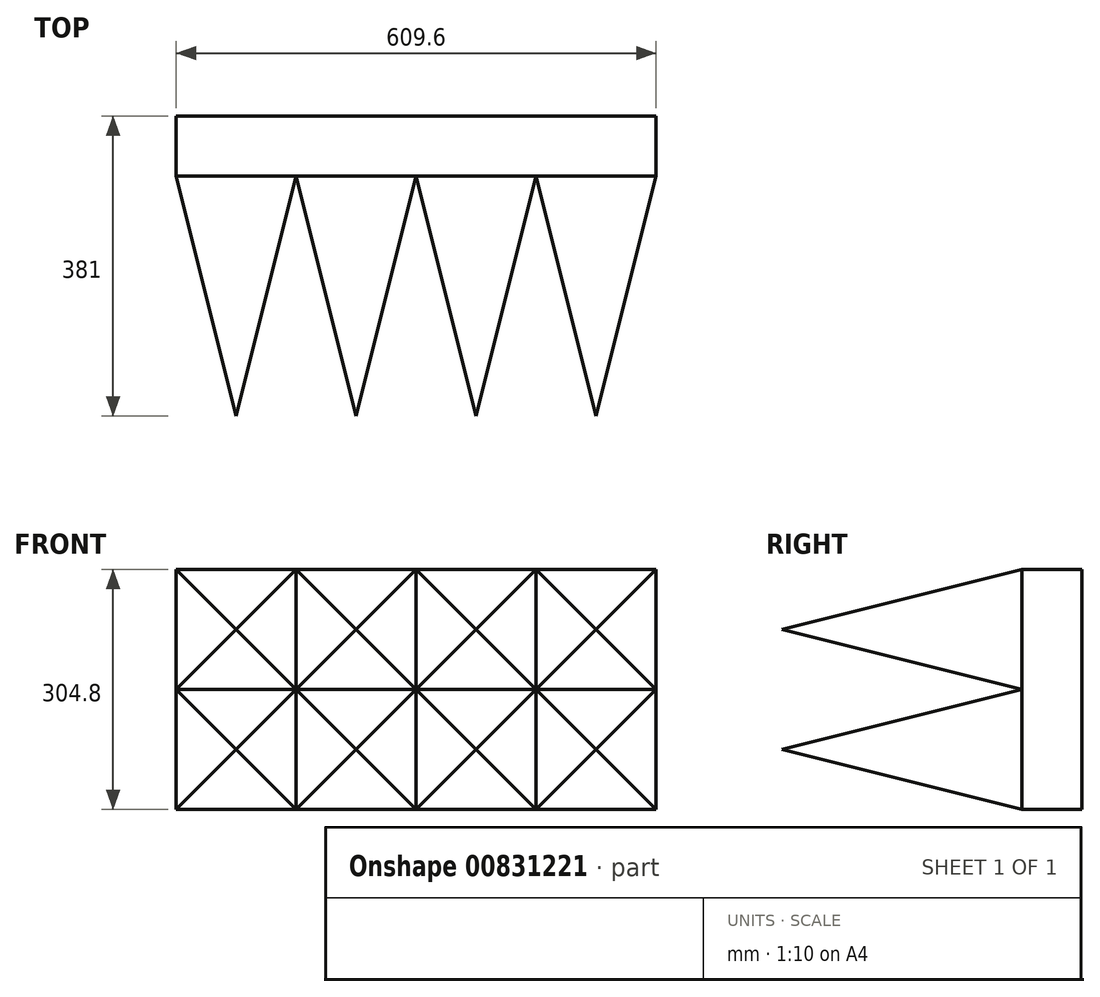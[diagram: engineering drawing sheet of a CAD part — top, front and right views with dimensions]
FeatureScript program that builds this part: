
annotation { "Feature Type Name" : "Feature", "Feature Type Description" : "" }
export const myFeature = defineFeature(function(context is Context, id is Id, definition is map)
    precondition{}
    {
        {
            var Q0;
            Q0=qCreatedBy(makeId("Front.planeOp"),FACE);
            var sketch = newSketch(context, id + "F0", { "sketchPlane" : qUnion([Q0])});
            skLineSegment(sketch, "E0.bottom", {"start": v(304.8, 152.4) * mm, "end": v(-304.8, 152.4) * mm});
            skLineSegment(sketch, "E0.top", {"start": v(304.8, -152.4) * mm, "end": v(-304.8, -152.4) * mm});
            skLineSegment(sketch, "E0.left", {"start": v(304.8, 152.4) * mm, "end": v(304.8, -152.4) * mm});
            skLineSegment(sketch, "E0.right", {"start": v(-304.8, 152.4) * mm, "end": v(-304.8, -152.4) * mm});
            skPoint(sketch, "E0.middle", {"position": v(0, 0) * mm});
            skSolve(sketch);
        }
        {
            var Q0;
            Q0=qSketchRegion(id+"F0",true);
            extrude(context, id + "F1", {"entities" : qUnion([Q0]), "depth" : 76.2 * mm});
        }
        {
            var Q0;
            Q0=qCreatedBy(makeId("Front.planeOp"),FACE);
            cPlane(context, id + "F2", {"entities" : qUnion([Q0]), "cplaneType" : CPlaneType.OFFSET, "offset" : 381 * mm, "width" : 152.4 * mm, "height" : 152.4 * mm});
        }
        {
            var Q0;
            Q0=makeQuery(id+"F1.opExtrude","CAP_FACE",FACE,{"disambiguationData":[OSD([sQuery(id+"F0.wireOp",EDGE,"E0.bottom"),sQuery(id+"F0.wireOp",EDGE,"E0.top"),sQuery(id+"F0.wireOp",EDGE,"E0.left"),sQuery(id+"F0.wireOp",EDGE,"E0.right")])],"isStart":false});
            var sketch = newSketch(context, id + "F3", { "sketchPlane" : qUnion([Q0])});
            skLineSegment(sketch, "E1.bottom", {"start": v(-152.4, 152.4) * mm, "end": v(-304.8, 152.4) * mm});
            skLineSegment(sketch, "E1.top", {"start": v(-152.4, 0) * mm, "end": v(-304.8, 0) * mm});
            skLineSegment(sketch, "E1.left", {"start": v(-152.4, 152.4) * mm, "end": v(-152.4, 0) * mm});
            skLineSegment(sketch, "E1.right", {"start": v(-304.8, 152.4) * mm, "end": v(-304.8, 0) * mm});
            skPoint(sketch, "E1.middle", {"position": v(-228.6, 76.2) * mm});
            skSolve(sketch);
        }
        {
            var Q0;
            Q0=qCreatedBy(id+"F2.planeOp",FACE);
            var sketch = newSketch(context, id + "F4", { "sketchPlane" : qUnion([Q0])});
            skPoint(sketch, "E2.0", {"position": v(-228.6, 76.2) * mm});
            skSolve(sketch);
        }
        {
            var Q1;
            Q1=makeQuery(id+"F3.imprint","IMPRINT",FACE,{"disambiguationData":[TD([[makeQuery(id+"F3.imprint","IMPRINT",EDGE,{"derivedFrom":sQuery(id+"F3.wireOp",EDGE,"E1.bottom")}),1.0]])]});
            var Q2;
            Q2=sQuery(id+"F4.wireOp",VERTEX,"E2.0");
            loft(context, id + "F5", {"operationType" : NewBodyOperationType.ADD, "sheetProfilesArray" : [{ "sheetProfileEntities" : qUnion([Q1]) }, { "sheetProfileEntities" : qUnion([Q2]) }]});
        }
        {
            var Q0;
            Q0=makeQuery(id+"F1.opExtrude","CAP_FACE",FACE,{"disambiguationData":[OSD([sQuery(id+"F0.wireOp",EDGE,"E0.bottom"),sQuery(id+"F0.wireOp",EDGE,"E0.top"),sQuery(id+"F0.wireOp",EDGE,"E0.left"),sQuery(id+"F0.wireOp",EDGE,"E0.right")])],"isStart":false});
            var sketch = newSketch(context, id + "F6", { "sketchPlane" : qUnion([Q0])});
            skLineSegment(sketch, "E3.bottom", {"start": v(0, 152.4) * mm, "end": v(-152.4, 152.4) * mm});
            skLineSegment(sketch, "E3.top", {"start": v(0, 0) * mm, "end": v(-152.4, 0) * mm});
            skLineSegment(sketch, "E3.left", {"start": v(0, 152.4) * mm, "end": v(0, 0) * mm});
            skLineSegment(sketch, "E3.right", {"start": v(-152.4, 152.4) * mm, "end": v(-152.4, 0) * mm});
            skPoint(sketch, "E3.middle", {"position": v(-76.2, 76.2) * mm});
            skSolve(sketch);
        }
        {
            var Q0;
            Q0=qCreatedBy(id+"F2.planeOp",FACE);
            var sketch = newSketch(context, id + "F7", { "sketchPlane" : qUnion([Q0])});
            skPoint(sketch, "E4.0", {"position": v(-76.2, 76.2) * mm});
            skSolve(sketch);
        }
        {
            var Q1;
            Q1=makeQuery(id+"F6.imprint","IMPRINT",FACE,{"disambiguationData":[TD([[makeQuery(id+"F6.imprint","IMPRINT",EDGE,{"derivedFrom":sQuery(id+"F6.wireOp",EDGE,"E3.bottom")}),1.0]])]});
            var Q2;
            Q2=sQuery(id+"F7.wireOp",VERTEX,"E4.0");
            loft(context, id + "F8", {"operationType" : NewBodyOperationType.ADD, "sheetProfilesArray" : [{ "sheetProfileEntities" : qUnion([Q1]) }, { "sheetProfileEntities" : qUnion([Q2]) }]});
        }
        {
            var Q0;
            Q0=makeQuery(id+"F1.opExtrude","CAP_FACE",FACE,{"disambiguationData":[OSD([sQuery(id+"F0.wireOp",EDGE,"E0.bottom"),sQuery(id+"F0.wireOp",EDGE,"E0.top"),sQuery(id+"F0.wireOp",EDGE,"E0.left"),sQuery(id+"F0.wireOp",EDGE,"E0.right")])],"isStart":false});
            var sketch = newSketch(context, id + "F9", { "sketchPlane" : qUnion([Q0])});
            skLineSegment(sketch, "E5.bottom", {"start": v(-152.4, 0) * mm, "end": v(-304.8, 0) * mm});
            skLineSegment(sketch, "E5.top", {"start": v(-152.4, -152.4) * mm, "end": v(-304.8, -152.4) * mm});
            skLineSegment(sketch, "E5.left", {"start": v(-152.4, 0) * mm, "end": v(-152.4, -152.4) * mm});
            skLineSegment(sketch, "E5.right", {"start": v(-304.8, 0) * mm, "end": v(-304.8, -152.4) * mm});
            skPoint(sketch, "E5.middle", {"position": v(-228.6, -76.2) * mm});
            skSolve(sketch);
        }
        {
            var Q0;
            Q0=qCreatedBy(id+"F2.planeOp",FACE);
            var sketch = newSketch(context, id + "F10", { "sketchPlane" : qUnion([Q0])});
            skPoint(sketch, "E6.0", {"position": v(-228.6, -76.2) * mm});
            skSolve(sketch);
        }
        {
            var Q1;
            Q1=makeQuery(id+"F9.imprint","IMPRINT",FACE,{"disambiguationData":[TD([[makeQuery(id+"F9.imprint","IMPRINT",EDGE,{"derivedFrom":sQuery(id+"F9.wireOp",EDGE,"E5.bottom")}),-1.0]])]});
            var Q2;
            Q2=sQuery(id+"F10.wireOp",VERTEX,"E6.0");
            loft(context, id + "F11", {"operationType" : NewBodyOperationType.ADD, "sheetProfilesArray" : [{ "sheetProfileEntities" : qUnion([Q1]) }, { "sheetProfileEntities" : qUnion([Q2]) }]});
        }
        {
            var Q0;
            Q0=makeQuery(id+"F1.opExtrude","CAP_FACE",FACE,{"disambiguationData":[OSD([sQuery(id+"F0.wireOp",EDGE,"E0.bottom"),sQuery(id+"F0.wireOp",EDGE,"E0.top"),sQuery(id+"F0.wireOp",EDGE,"E0.left"),sQuery(id+"F0.wireOp",EDGE,"E0.right")])],"isStart":false});
            var sketch = newSketch(context, id + "F12", { "sketchPlane" : qUnion([Q0])});
            skLineSegment(sketch, "E7.bottom", {"start": v(0, 0) * mm, "end": v(-152.4, 0) * mm});
            skLineSegment(sketch, "E7.top", {"start": v(0, -152.4) * mm, "end": v(-152.4, -152.4) * mm});
            skLineSegment(sketch, "E7.left", {"start": v(0, 0) * mm, "end": v(0, -152.4) * mm});
            skLineSegment(sketch, "E7.right", {"start": v(-152.4, 0) * mm, "end": v(-152.4, -152.4) * mm});
            skPoint(sketch, "E7.middle", {"position": v(-76.2, -76.2) * mm});
            skSolve(sketch);
        }
        {
            var Q0;
            Q0=qCreatedBy(id+"F2.planeOp",FACE);
            var sketch = newSketch(context, id + "F13", { "sketchPlane" : qUnion([Q0])});
            skPoint(sketch, "E8.0", {"position": v(-76.2, -76.2) * mm});
            skSolve(sketch);
        }
        {
            var Q1;
            Q1=makeQuery(id+"F12.imprint","IMPRINT",FACE,{"disambiguationData":[TD([[makeQuery(id+"F12.imprint","IMPRINT",EDGE,{"derivedFrom":sQuery(id+"F12.wireOp",EDGE,"E7.bottom")}),-1.0]])]});
            var Q2;
            Q2=sQuery(id+"F13.wireOp",VERTEX,"E8.0");
            loft(context, id + "F14", {"operationType" : NewBodyOperationType.ADD, "sheetProfilesArray" : [{ "sheetProfileEntities" : qUnion([Q1]) }, { "sheetProfileEntities" : qUnion([Q2]) }]});
        }
        {
            var Q0;
            Q0=makeQuery(id+"F1.opExtrude","SWEPT_BODY",BODY,{"disambiguationData":[OSD([sQuery(id+"F0.wireOp",EDGE,"E0.bottom"),sQuery(id+"F0.wireOp",EDGE,"E0.top"),sQuery(id+"F0.wireOp",EDGE,"E0.left"),sQuery(id+"F0.wireOp",EDGE,"E0.right")])]});
            var Q1;
            Q1=qCreatedBy(makeId("Right.planeOp"),FACE);
            mirror(context, id + "F15", {"operationType" : NewBodyOperationType.ADD, "entities" : qUnion([Q0]), "mirrorPlane" : qUnion([Q1])});
        }
    });
